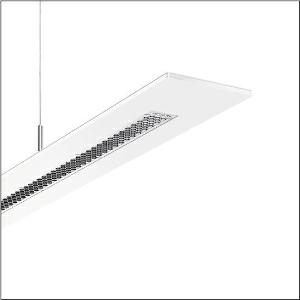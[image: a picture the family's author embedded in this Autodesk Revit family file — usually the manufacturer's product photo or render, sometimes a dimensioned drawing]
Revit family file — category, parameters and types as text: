
# Revit family: arktika_r__21_5mb251dl30840_e160
name_source: partatom
category: Lighting Fixtures
units: mm (PartAtom-declared; Revit-internal decimal feet)

## family parameters
Cut with Voids When Loaded = No
Host = Face
Light Source = No
Part Type = Normal
Room Calculation Point = No
Round Connector Dimension = Use Diameter
Shared = No

## types (1)
- --- (1 x LED 4000K / CRI = 80 (unbekannt), 4400 lm, 4000K)
    Apparent Load = 34 VA
    CIE Flux Codes = 81 100 100 79 100
    Color Rendering = 80
    Color Temperature = 4000K
    Default Elevation = 1800 mm
    Description = Arktika® 21, office luminaire, primary anti-glare with honeycomb louvre, of plastic, aluminium vaporised, highly specular, light emission: direct/indirect distribution, primary light characteristic: symmetric, installation type: suspended mounting, LED, rated luminous flux: 4.400lm, luminous efficacy: 131lm/W, light colour: 840, colour temperature: 4000K, control gear: ECG DALI, with terminal, 3+2-pole, max. 2.5mm², mains connection: 220..240V, AC, 50/60Hz, rated input power: 34W, housing, of aluminium, powder-coated, traffic white (RAL 9016), 1-length, length: 1.250mm, width: 120mm, height: 8mm, protection rating (complete): IP20, insulation class (complete): insulation class II (safety insulation), certification: CE, ENEC, VDE, packaging unit: 1 piece
    Height = 8 mm  [stored 0.0262467 ft]
    Lamp = 1 x LED 4000K / CRI >= 80 (unbekannt)
    Lamp Light Flux = 4400 lm
    Lamp count = 1
    Length = 1250 mm
    Luminous efficacy = 131 lm/W
    Manufacturer = Siteco
    ModVariant = No
    Model = 5MB251DL30840
    Mounting Place = Ceiling
    Mounting Type = Pendant
    Number of Poles = 1
    OnlyDefault = Yes
    Power Factor = 1
    Product Name = Arktika® 21
    Product group = office luminaire | ceiling pendant
    ProductGroupID = 902
    Protection Class = Protection class II
    Protection Degree = IP 20
    RLX_Detail_Level = 1
    RLX_Emergency_Light_Flux = 0 lm
    RLX_Emergency_Type = 0
    RLX_Emergency_Type_DB = No
    RlxData = <blob elided: 39341 chars, md5=8b75a79a>
    Socket = socket
    Standby Power = 0 W
    System Light Flux = 4400 lm
    System Power = 34 W
    Type Comments = factory setting: luminous flux: 100 % | dim-lin: 254 | 665 mA
    Type Image = l_1006128.jpg
    URL = http://relux.com
    VarID = @adj_164557
    Voltage = 0 V
    Weight = 0.00 kg
    Width = 120 mm

note: [stored X ft] marks values corroborated as IEEE doubles in the binary element streams (Revit-internal decimal feet)

## geometry (parser evidence)
native form markers: Blend x4, Sweep x12
no freeform markers — native parametric forms only
